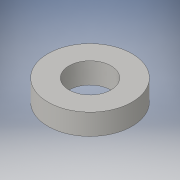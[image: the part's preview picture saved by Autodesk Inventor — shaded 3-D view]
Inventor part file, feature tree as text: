
AUTODESK INVENTOR PART (.ipt)
format: ipt  version: 2016 (Build 200138000, 138)  size: 108,032 bytes
history: native  units: in
note: dims shown in document units (in); Inventor stores cm internally (conversion verified against a paired STEP export)
features: extrude x1, sketch x1
ambient origin geometry x8: Origin, YZ Plane, XZ Plane, XY Plane, X Axis, Y Axis, Z Axis, Center Point
bodies: Solid1 (feature_tree)
feature tree (2):
  extrude  "Extrusion1"  Depth=0.25in
  sketch  "Sketch1"  dims[d0=0.5in d1=1.0in d2=0.25in d3=0.0in]
